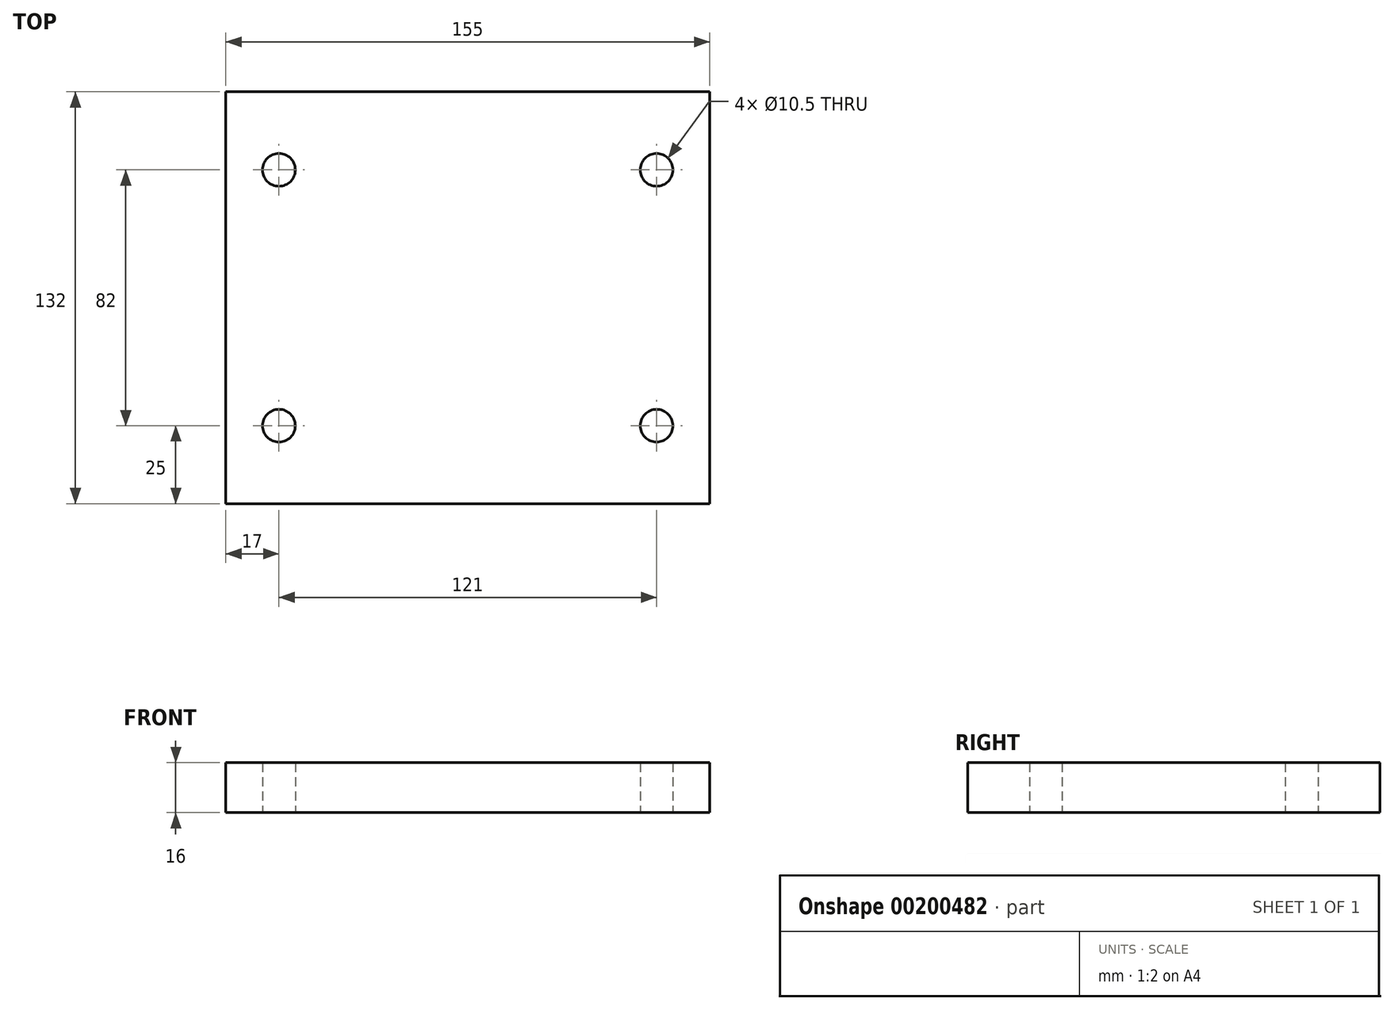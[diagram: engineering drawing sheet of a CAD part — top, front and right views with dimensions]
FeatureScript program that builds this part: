
annotation { "Feature Type Name" : "Feature", "Feature Type Description" : "" }
export const myFeature = defineFeature(function(context is Context, id is Id, definition is map)
    precondition{}
    {
        {
            var Q0;
            Q0=qCreatedBy(makeId("Top.planeOp"),FACE);
            var sketch = newSketch(context, id + "F0", { "sketchPlane" : qUnion([Q0])});
            skLineSegment(sketch, "E0.bottom", {"start": v(-77.5, 66) * mm, "end": v(77.5, 66) * mm});
            skLineSegment(sketch, "E0.top", {"start": v(-77.5, -66) * mm, "end": v(77.5, -66) * mm});
            skLineSegment(sketch, "E0.left", {"start": v(-77.5, 66) * mm, "end": v(-77.5, -66) * mm});
            skLineSegment(sketch, "E0.right", {"start": v(77.5, 66) * mm, "end": v(77.5, -66) * mm});
            skPoint(sketch, "E0.middle", {"position": v(0, 0) * mm});
            skCircle(sketch, "E1", {"center": v(-60.5, 41) * mm, "radius": 5.25 * mm});
            skCircle(sketch, "E2.MirrorC", {"center": v(-60.5, -41) * mm, "radius": 5.25 * mm});
            skCircle(sketch, "E3.MirrorC", {"center": v(60.5, 41) * mm, "radius": 5.25 * mm});
            skCircle(sketch, "E4.MirrorC", {"center": v(60.5, -41) * mm, "radius": 5.25 * mm});
            skSolve(sketch);
        }
        {
            var Q0;
            Q0=makeQuery(id+"F0.imprint","IMPRINT",FACE,{"disambiguationData":[TD([[makeQuery(id+"F0.imprint","IMPRINT",EDGE,{"derivedFrom":sQuery(id+"F0.wireOp",EDGE,"E0.bottom")}),-1.0]])]});
            extrude(context, id + "F1", {"entities" : qUnion([Q0]), "depth" : 16 * mm});
        }
    });
